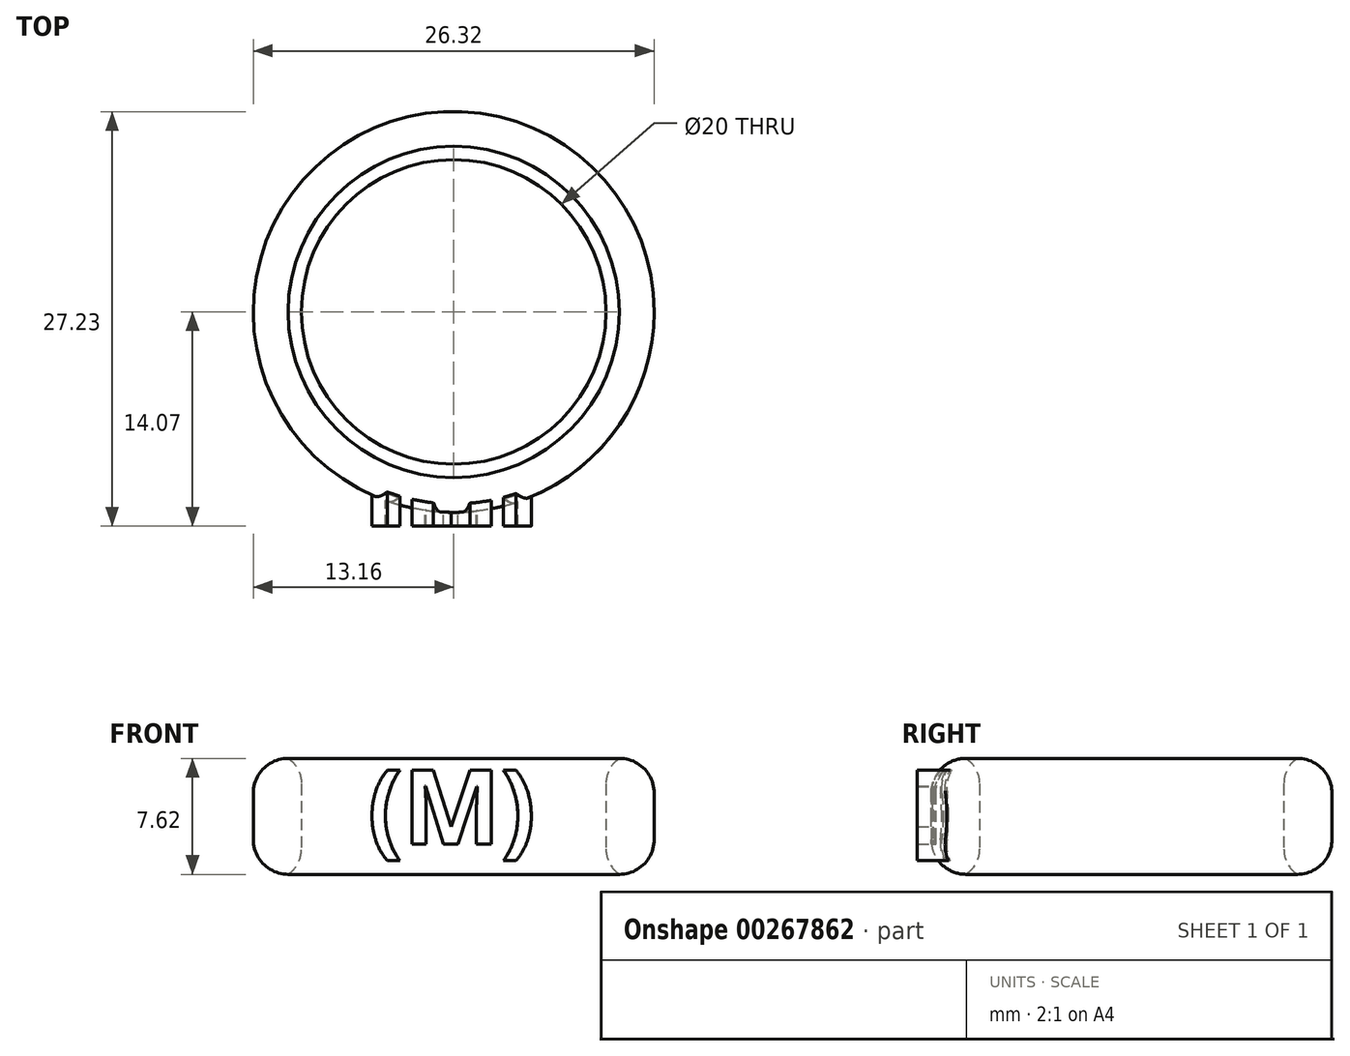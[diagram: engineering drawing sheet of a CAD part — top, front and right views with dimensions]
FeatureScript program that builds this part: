
annotation { "Feature Type Name" : "Feature", "Feature Type Description" : "" }
export const myFeature = defineFeature(function(context is Context, id is Id, definition is map)
    precondition{}
    {
        {
            var Q0;
            Q0=qCreatedBy(makeId("Top.planeOp"),FACE);
            var sketch = newSketch(context, id + "F0", { "sketchPlane" : qUnion([Q0])});
            skCircle(sketch, "E0", {"center": v(0, 0) * mm, "radius": 10 * mm});
            skCircle(sketch, "E1", {"center": v(0, 0) * mm, "radius": 13.16 * mm});
            skSolve(sketch);
        }
        {
            var Q0;
            Q0=makeQuery(id+"F0.imprint","IMPRINT",FACE,{"disambiguationData":[TD([[makeQuery(id+"F0.imprint","IMPRINT",EDGE,{"derivedFrom":sQuery(id+"F0.wireOp",EDGE,"E0")}),-1.0]])]});
            extrude(context, id + "F1", {"entities" : qUnion([Q0]), "endBound" : BoundingType.SYMMETRIC, "depth" : 7.62 * mm});
        }
        {
            var Q0;
            Q0=makeQuery(id+"F1.opExtrude","CAP_EDGE",EDGE,{"disambiguationData":[OSD([sQuery(id+"F0.wireOp",EDGE,"E1")])],"isStart":true});
            fillet(context, id + "F2", {"entities" : qUnion([Q0]), "radius" : 2.3 * mm, "tangentPropagation" : true, "allowEdgeOverflow" : false});
        }
        {
            var Q0;
            Q0=makeQuery(id+"F1.opExtrude","CAP_EDGE",EDGE,{"disambiguationData":[OSD([sQuery(id+"F0.wireOp",EDGE,"E1")])],"isStart":false});
            fillet(context, id + "F3", {"entities" : qUnion([Q0]), "radius" : 2.3 * mm, "tangentPropagation" : true, "allowEdgeOverflow" : false});
        }
        {
            var Q0;
            Q0=makeQuery(id+"F1.opExtrude","CAP_EDGE",EDGE,{"disambiguationData":[OSD([sQuery(id+"F0.wireOp",EDGE,"E0")])],"isStart":true});
            fillet(context, id + "F4", {"entities" : qUnion([Q0]), "radius" : 2.03 * mm, "tangentPropagation" : true, "allowEdgeOverflow" : false});
        }
        {
            var Q0;
            Q0=makeQuery(id+"F1.opExtrude","CAP_EDGE",EDGE,{"disambiguationData":[OSD([sQuery(id+"F0.wireOp",EDGE,"E0")])],"isStart":false});
            fillet(context, id + "F5", {"entities" : qUnion([Q0]), "radius" : 2.03 * mm, "tangentPropagation" : true, "allowEdgeOverflow" : false});
        }
        {
            var Q0;
            Q0=qCreatedBy(makeId("Front.planeOp"),FACE);
            cPlane(context, id + "F6", {"entities" : qUnion([Q0]), "cplaneType" : CPlaneType.OFFSET, "offset" : 10.26 * mm, "width" : 152.4 * mm, "height" : 152.4 * mm});
        }
        {
            var Q0;
            Q0=qCreatedBy(id+"F6.planeOp",FACE);
            var sketch = newSketch(context, id + "F7", { "sketchPlane" : qUnion([Q0])});
            skText(sketch, "E2", { "text": "(M)", "fontName": "OpenSans-Bold.ttf"});
            const initialGuessF7  = {"E2": [-0.00564, -0.00183, 1, 0, 0.00489]};
            skSetInitialGuess(sketch, initialGuessF7);
            skSolve(sketch);
        }
        {
            var Q0;
            Q0 = qSketchRegion(id + "F7", true);
            extrude(context, id + "F8", {"entities" : qUnion([Q0]), "operationType" : NewBodyOperationType.ADD, "depth" : 3.8 * mm});
        }
    });
